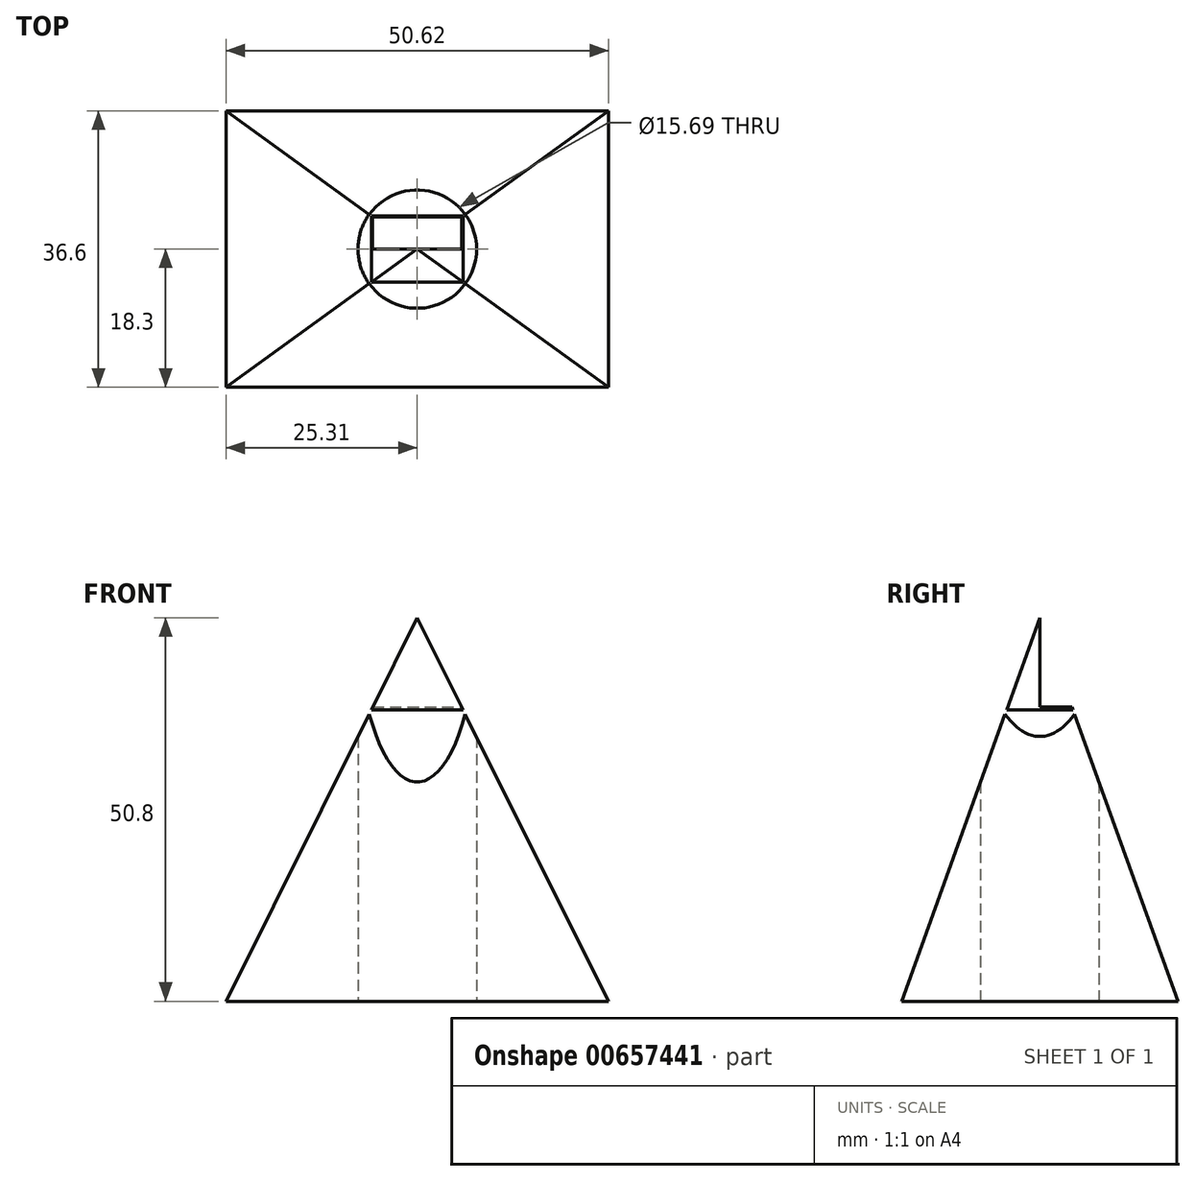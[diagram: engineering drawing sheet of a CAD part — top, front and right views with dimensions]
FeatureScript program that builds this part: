
annotation { "Feature Type Name" : "Feature", "Feature Type Description" : "" }
export const myFeature = defineFeature(function(context is Context, id is Id, definition is map)
    precondition{}
    {
        {
            var Q0;
            Q0=qCreatedBy(makeId("Top.planeOp"),FACE);
            var sketch = newSketch(context, id + "F0", { "sketchPlane" : qUnion([Q0])});
            skLineSegment(sketch, "E0.bottom", {"start": v(-25.31, 18.3) * mm, "end": v(25.31, 18.3) * mm});
            skLineSegment(sketch, "E0.top", {"start": v(-25.31, -18.3) * mm, "end": v(25.31, -18.3) * mm});
            skLineSegment(sketch, "E0.left", {"start": v(-25.31, 18.3) * mm, "end": v(-25.31, -18.3) * mm});
            skLineSegment(sketch, "E0.right", {"start": v(25.31, 18.3) * mm, "end": v(25.31, -18.3) * mm});
            skPoint(sketch, "E0.middle", {"position": v(0, 0) * mm});
            skSolve(sketch);
        }
        {
            var Q0;
            Q0=qCreatedBy(makeId("Top.planeOp"),FACE);
            cPlane(context, id + "F1", {"entities" : qUnion([Q0]), "cplaneType" : CPlaneType.OFFSET, "offset" : 50.8 * mm, "width" : 152.4 * mm, "height" : 152.4 * mm});
        }
        {
            var Q0;
            Q0=qCreatedBy(id+"F1.planeOp",FACE);
            var sketch = newSketch(context, id + "F2", { "sketchPlane" : qUnion([Q0])});
            skPoint(sketch, "E1", {"position": v(0, 0) * mm});
            skSolve(sketch);
        }
        {
            var Q0;
            Q0=sQuery(id+"F2.wireOp",VERTEX,"E1");
            var Q1;
            Q1=makeQuery(id+"F0.imprint","IMPRINT",FACE,{"disambiguationData":[TD([[makeQuery(id+"F0.imprint","IMPRINT",EDGE,{"derivedFrom":sQuery(id+"F0.wireOp",EDGE,"E0.bottom")}),-1.0]])]});
            loft(context, id + "F3", {"sheetProfilesArray" : [{ "sheetProfileEntities" : qUnion([Q0]) }, { "sheetProfileEntities" : qUnion([Q1]) }]});
        }
        {
            var Q0;
            Q0=qCreatedBy(makeId("Front.planeOp"),FACE);
            var sketch = newSketch(context, id + "F4", { "sketchPlane" : qUnion([Q0])});
            skLineSegment(sketch, "E2.bottom", {"start": v(24.93, 38.96) * mm, "end": v(-24.93, 38.96) * mm});
            skLineSegment(sketch, "E2.top", {"start": v(24.93, 72.33) * mm, "end": v(-24.93, 72.33) * mm});
            skLineSegment(sketch, "E2.left", {"start": v(24.93, 38.96) * mm, "end": v(24.93, 72.33) * mm});
            skLineSegment(sketch, "E2.right", {"start": v(-24.93, 38.96) * mm, "end": v(-24.93, 72.33) * mm});
            skPoint(sketch, "E2.middle", {"position": v(0, 55.65) * mm});
            skSolve(sketch);
        }
        {
            var Q0;
            Q0=makeQuery(id+"F4.imprint","IMPRINT",FACE,{"disambiguationData":[TD([[makeQuery(id+"F4.imprint","IMPRINT",EDGE,{"derivedFrom":sQuery(id+"F4.wireOp",EDGE,"E2.bottom")}),-1.0]])]});
            extrude(context, id + "F5", {"entities" : qUnion([Q0]), "operationType" : NewBodyOperationType.REMOVE, "oppositeDirection" : true, "depth" : 127 * mm, "offsetDistance" : 25.4 * mm});
        }
        {
            var Q0;
            Q0=makeQuery(id+"F3.opLoft","CAP_FACE",FACE,{"disambiguationData":[OSD([makeQuery(id+"F0.imprint","IMPRINT",FACE,{"disambiguationData":[TD([[makeQuery(id+"F0.imprint","IMPRINT",EDGE,{"derivedFrom":sQuery(id+"F0.wireOp",EDGE,"E0.bottom")}),-1.0]])]})])],"isStart":true});
            var sketch = newSketch(context, id + "F6", { "sketchPlane" : qUnion([Q0])});
            skCircle(sketch, "E3", {"center": v(0, 0) * mm, "radius": 7.85 * mm});
            skSolve(sketch);
        }
        {
            var Q0;
            Q0=makeQuery(id+"F6.imprint","IMPRINT",FACE,{"disambiguationData":[TD([[makeQuery(id+"F6.imprint","IMPRINT",EDGE,{"derivedFrom":sQuery(id+"F6.wireOp",EDGE,"E3")}),1.0]])]});
            extrude(context, id + "F7", {"entities" : qUnion([Q0]), "operationType" : NewBodyOperationType.REMOVE, "oppositeDirection" : true, "depth" : 38.6 * mm, "offsetDistance" : 25.4 * mm});
        }
    });
